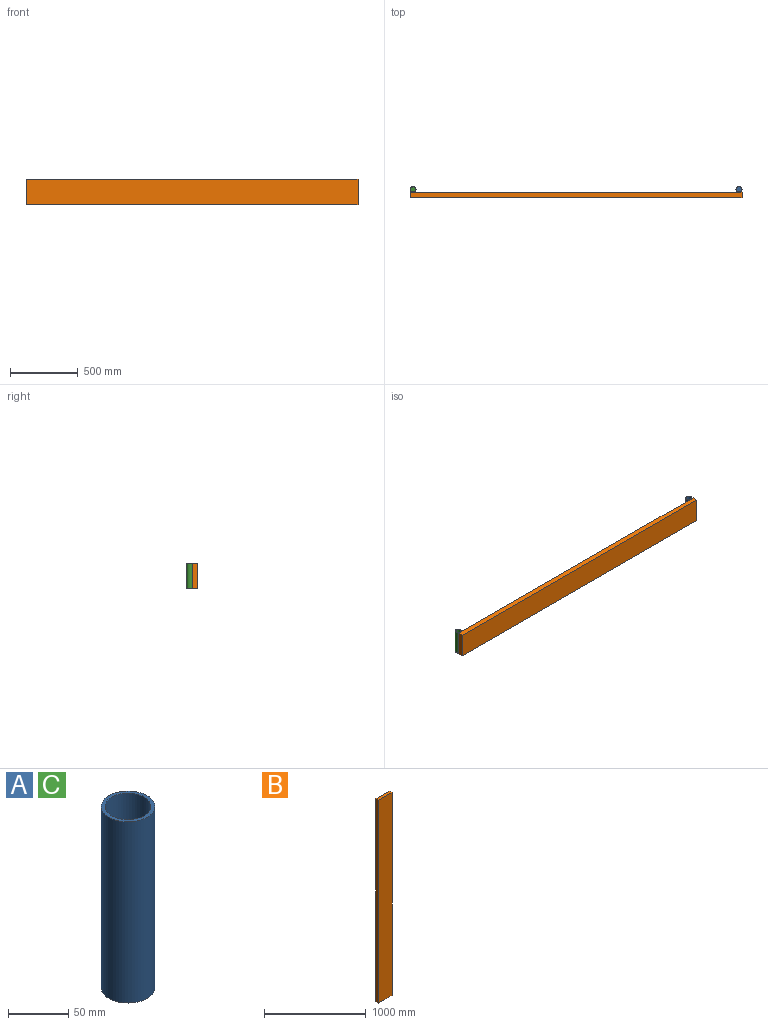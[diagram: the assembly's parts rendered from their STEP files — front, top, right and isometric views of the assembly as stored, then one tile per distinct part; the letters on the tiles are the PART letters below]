
ASSEMBLY  parts=3 mates=1
PART A: 5 faces, bbox 44.5x44.5x184.2 mm
  f0: cylinder r=22.23mm len=184.15mm, axis (0,0,-1), area 25715.4mm2, adj f1,f2
  f1: plane 44.45x44.45mm, normal (0,0,1), area 411.7mm2, adj f0,f3
  f2: plane 44.45x44.45mm, normal (0,0,-1), area 1551.8mm2, adj f0
  f3: cylinder r=19.05mm len=180.98mm, axis (0,0,-1), area 21661.7mm2, adj f1,f4
  f4: plane 38.1x38.1mm, normal (0,0,1), area 1140.1mm2, adj f3
PART B: 6 faces, bbox 184.2x38.1x2438.4 mm
  f0: plane 2438.4x38.1mm, normal (-1,0,0), area 92903mm2, adj f1,f3,f4,f5
  f1: plane 2438.4x184.15mm, normal (0,-1,0), area 449031.4mm2, adj f0,f2,f4,f5
  f2: plane 2438.4x38.1mm, normal (1,0,0), area 92903mm2, adj f1,f3,f4,f5
  f3: plane 2438.4x184.15mm, normal (0,1,0), area 449031.4mm2, adj f0,f2,f4,f5
  f4: plane 184.15x38.1mm, normal (0,0,1), area 7016.1mm2, adj f0,f1,f2,f3
  f5: plane 184.15x38.1mm, normal (0,0,-1), area 7016.1mm2, adj f0,f1,f2,f3
PART C: same geometry as A
PLACE A rot(axis=(0.71,-0.22,0.67),0deg) t=(-22.23,22.22,0)mm
PLACE B rot(axis=(0.71,0,-0.71),180deg) t=(0,0,184.15)mm
PLACE C rot(axis=(0.71,-0.22,0.67),0deg) t=(-2419.35,22.23,0)mm
MATE fastened B.f2 <-> A.f2  axis (0,0,-1) through (0,-38.1,0)mm
